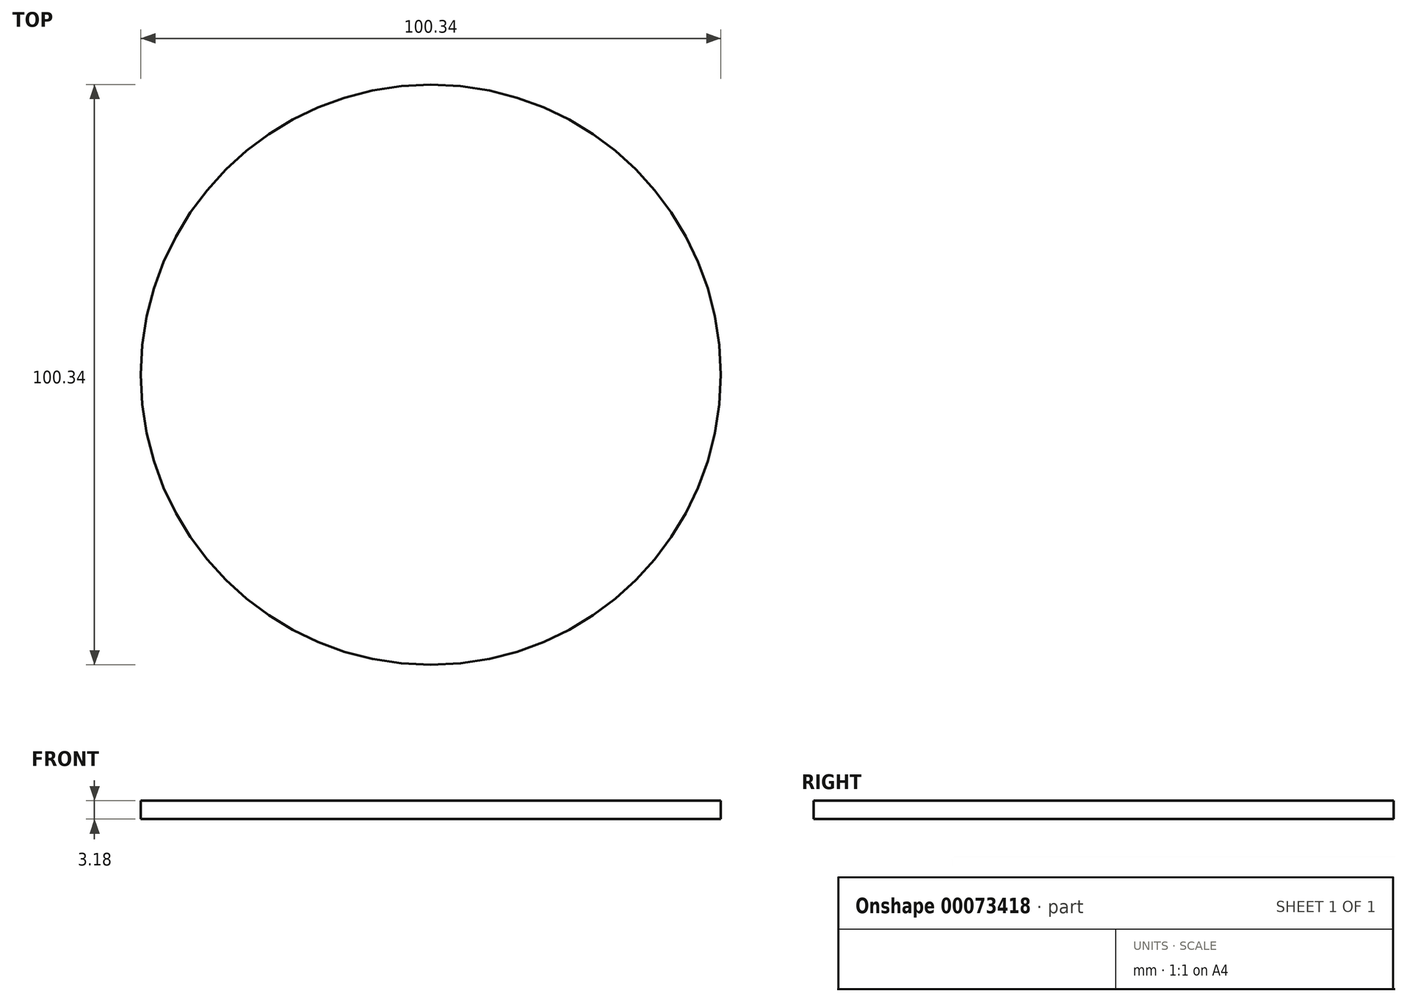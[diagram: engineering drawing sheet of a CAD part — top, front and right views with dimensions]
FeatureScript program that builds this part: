
annotation { "Feature Type Name" : "Feature", "Feature Type Description" : "" }
export const myFeature = defineFeature(function(context is Context, id is Id, definition is map)
    precondition{}
    {
        {
            var Q0;
            Q0=qCreatedBy(makeId("Top.planeOp"),FACE);
            var sketch = newSketch(context, id + "F0", { "sketchPlane" : qUnion([Q0])});
            skCircle(sketch, "E0", {"center": v(0, 0) * mm, "radius": 50.16 * mm});
            skSolve(sketch);
        }
        {
            var Q0;
            Q0=makeQuery(id+"F0.imprint","IMPRINT",FACE,{"disambiguationData":[TD([[makeQuery(id+"F0.imprint","IMPRINT",EDGE,{"derivedFrom":sQuery(id+"F0.wireOp",EDGE,"E0")}),1.0]])]});
            extrude(context, id + "F1", {"entities" : qUnion([Q0]), "depth" : 3.17 * mm});
        }
    });
